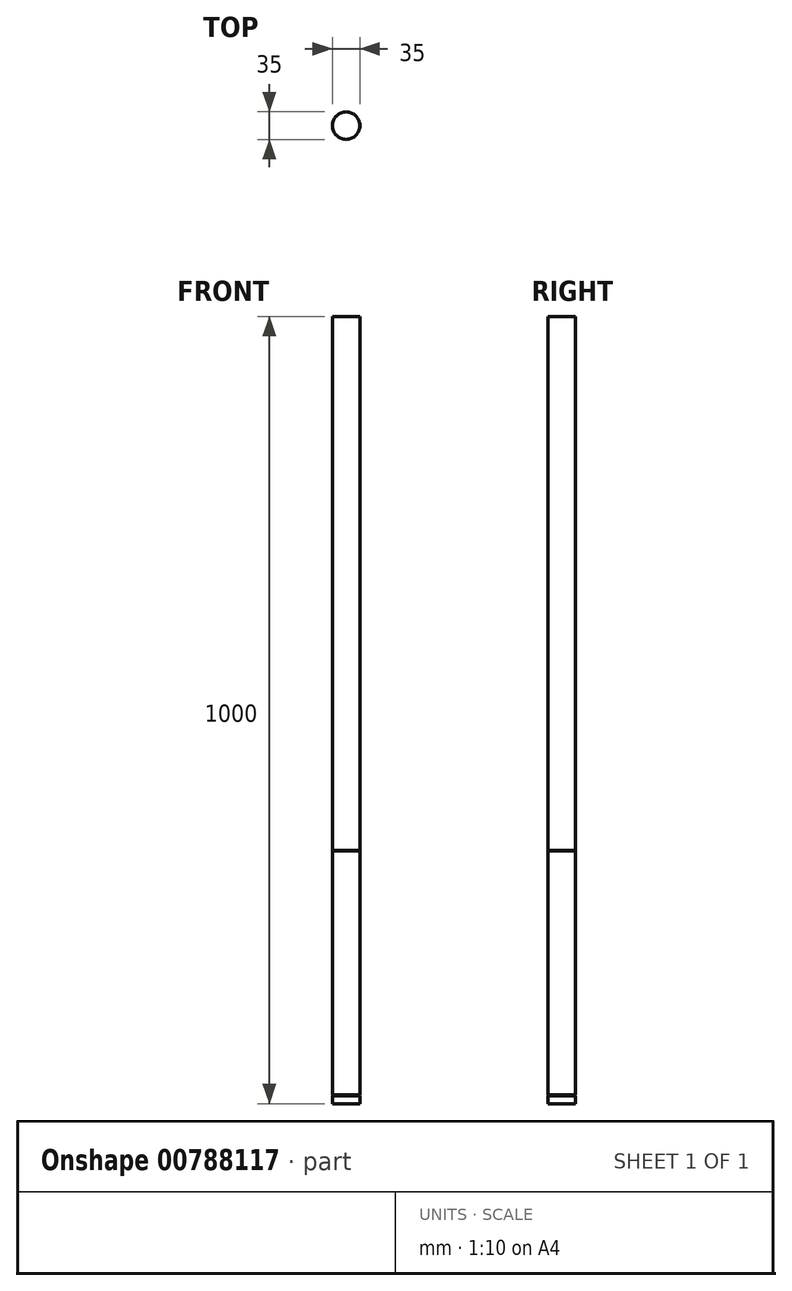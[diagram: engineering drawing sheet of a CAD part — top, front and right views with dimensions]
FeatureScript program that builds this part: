
annotation { "Feature Type Name" : "Feature", "Feature Type Description" : "" }
export const myFeature = defineFeature(function(context is Context, id is Id, definition is map)
    precondition{}
    {
        {
            var Q0;
            Q0=qCreatedBy(makeId("Front.planeOp"),FACE);
            var sketch = newSketch(context, id + "F0", { "sketchPlane" : qUnion([Q0])});
            skLineSegment(sketch, "E0", {"start": v(0, 0) * mm, "end": v(-17.5, 0) * mm});
            skLineSegment(sketch, "E1", {"start": v(-17.5, 0) * mm, "end": v(-17.5, 10) * mm});
            skLineSegment(sketch, "E2", {"start": v(-17.5, 1000) * mm, "end": v(0, 1000) * mm});
            skLineSegment(sketch, "E3", {"start": v(0, 1000) * mm, "end": v(0, 0) * mm});
            skLineSegment(sketch, "E4", {"start": v(-17.5, 10) * mm, "end": v(-16.5, 10) * mm});
            skLineSegment(sketch, "E5", {"start": v(-16.5, 10) * mm, "end": v(-16.5, 11) * mm});
            skLineSegment(sketch, "E6", {"start": v(-16.5, 11) * mm, "end": v(-17.5, 11) * mm});
            skLineSegment(sketch, "E7.trimOffspring", {"start": v(-17.5, 11) * mm, "end": v(-17.5, 321) * mm});
            skLineSegment(sketch, "E8", {"start": v(-17.5, 321) * mm, "end": v(-16.5, 321) * mm});
            skLineSegment(sketch, "E9", {"start": v(-16.5, 321) * mm, "end": v(-16.5, 322) * mm});
            skLineSegment(sketch, "E10", {"start": v(-16.5, 322) * mm, "end": v(-17.5, 322) * mm});
            skLineSegment(sketch, "E11.trimOffspring", {"start": v(-17.5, 322) * mm, "end": v(-17.5, 1000) * mm});
            skLineSegment(sketch, "E12", {"start": v(0, -250.16) * mm, "end": v(0, 1056.72) * mm, "construction": true});
            skSolve(sketch);
        }
        {
            var Q0;
            Q0 = qSketchRegion(id + "F0", true);
            var Q1;
            Q1=sQuery(id+"F0.wireOp",EDGE,"E12");
            revolve(context, id + "F1", {"surfaceOperationType" : NewSurfaceOperationType.NEW, "entities" : qUnion([Q0]), "axis" : qUnion([Q1]), "revolveType" : RevolveType.FULL});
        }
    });
